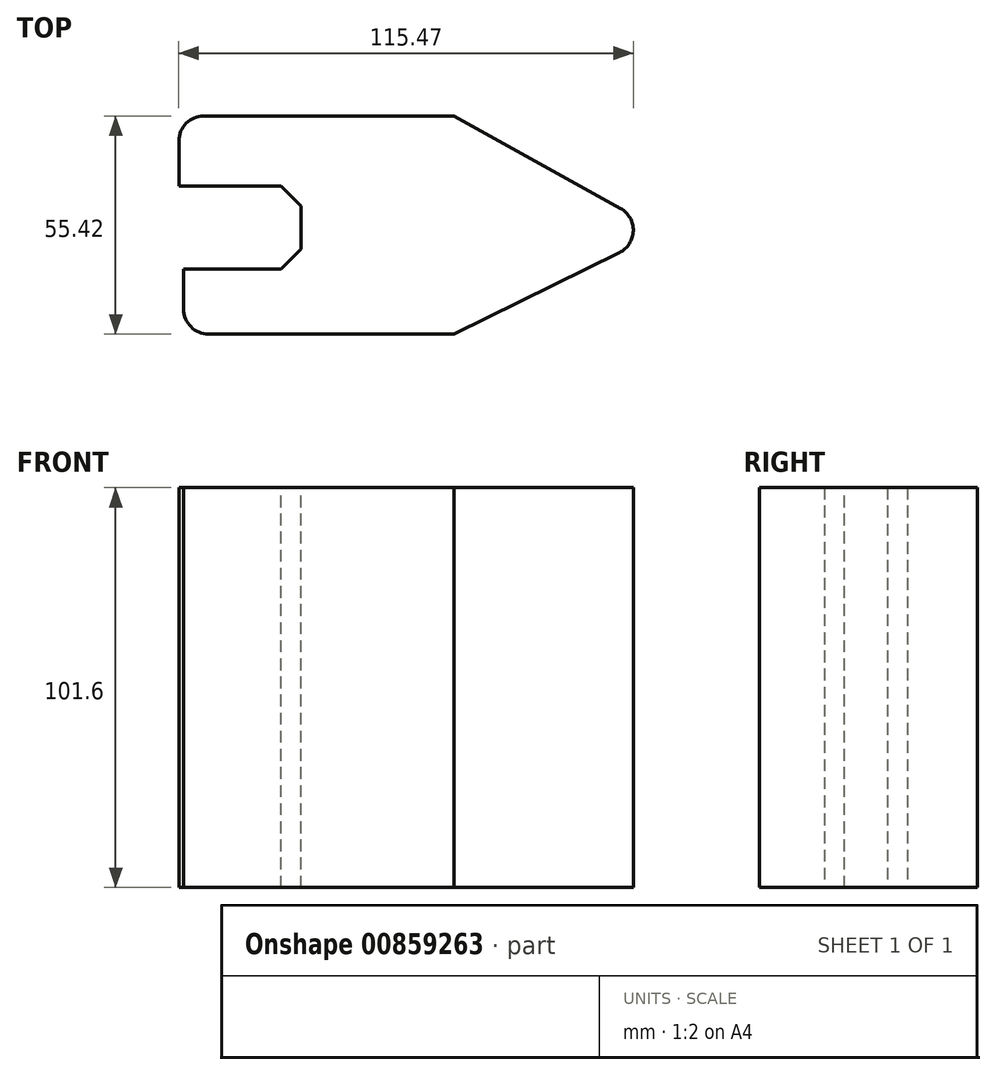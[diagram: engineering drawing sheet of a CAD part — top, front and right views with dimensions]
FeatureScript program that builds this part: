
annotation { "Feature Type Name" : "Feature", "Feature Type Description" : "" }
export const myFeature = defineFeature(function(context is Context, id is Id, definition is map)
    precondition{}
    {
        {
            var Q0;
            Q0=qCreatedBy(makeId("Top.planeOp"),FACE);
            var sketch = newSketch(context, id + "F0", { "sketchPlane" : qUnion([Q0])});
            skLineSegment(sketch, "E0", {"start": v(-122.8, 29.35) * mm, "end": v(-52.91, 29.35) * mm});
            skLineSegment(sketch, "E1", {"start": v(-52.91, 29.35) * mm, "end": v(0, 0) * mm});
            skLineSegment(sketch, "E2", {"start": v(0, 0) * mm, "end": v(-52.91, -26.07) * mm});
            skLineSegment(sketch, "E3", {"start": v(-52.91, -26.07) * mm, "end": v(-121.57, -26.07) * mm});
            skLineSegment(sketch, "E4", {"start": v(-121.57, -26.07) * mm, "end": v(-121.57, -9.52) * mm});
            skLineSegment(sketch, "E5", {"start": v(-121.57, -9.52) * mm, "end": v(-91.79, -9.52) * mm});
            skLineSegment(sketch, "E6", {"start": v(-91.79, -9.52) * mm, "end": v(-91.79, 11.57) * mm});
            skLineSegment(sketch, "E7", {"start": v(-91.79, 11.57) * mm, "end": v(-122.8, 11.57) * mm});
            skLineSegment(sketch, "E8", {"start": v(-122.8, 11.57) * mm, "end": v(-122.8, 29.35) * mm});
            skSolve(sketch);
        }
        {
            var Q0;
            Q0 = qSketchRegion(id + "F0", true);
            extrude(context, id + "F1", {"entities" : qUnion([Q0]), "depth" : 101.6 * mm, "offsetDistance" : 25.4 * mm});
        }
        {
            var Q0;
            Q0=makeQuery(id+"F1.opExtrude","SWEPT_EDGE",EDGE,{"disambiguationData":[OSD([sQuery(id+"F0.wireOp",EDGE,"E3"),sQuery(id+"F0.wireOp",EDGE,"E4")])]});
            var Q1;
            Q1=makeQuery(id+"F1.opExtrude","SWEPT_EDGE",EDGE,{"disambiguationData":[OSD([sQuery(id+"F0.wireOp",EDGE,"E0"),sQuery(id+"F0.wireOp",EDGE,"E8")])]});
            fillet(context, id + "F2", {"entities" : qUnion([Q0, Q1]), "radius" : 6.35 * mm, "tangentPropagation" : true, "allowEdgeOverflow" : false});
        }
        {
            var Q0;
            Q0=makeQuery(id+"F1.opExtrude","SWEPT_EDGE",EDGE,{"disambiguationData":[OSD([sQuery(id+"F0.wireOp",EDGE,"E6"),sQuery(id+"F0.wireOp",EDGE,"E7")])]});
            chamfer(context, id + "F3", {"entities" : qUnion([Q0]), "chamferType" : ChamferType.TWO_OFFSETS, "width1" : 5.08 * mm, "oppositeDirection" : false, "width2" : 5.08 * mm, "tangentPropagation" : true});
        }
        {
            var Q0;
            Q0=makeQuery(id+"F1.opExtrude","SWEPT_EDGE",EDGE,{"disambiguationData":[OSD([sQuery(id+"F0.wireOp",EDGE,"E5"),sQuery(id+"F0.wireOp",EDGE,"E6")])]});
            chamfer(context, id + "F4", {"entities" : qUnion([Q0]), "chamferType" : ChamferType.TWO_OFFSETS, "width1" : 5.08 * mm, "oppositeDirection" : false, "width2" : 5.08 * mm, "tangentPropagation" : true});
        }
        {
            var Q0;
            Q0=makeQuery(id+"F1.opExtrude","SWEPT_EDGE",EDGE,{"disambiguationData":[OSD([sQuery(id+"F0.wireOp",EDGE,"E1"),sQuery(id+"F0.wireOp",EDGE,"E2")])]});
            fillet(context, id + "F5", {"entities" : qUnion([Q0]), "radius" : 6.35 * mm, "tangentPropagation" : true, "allowEdgeOverflow" : false});
        }
    });
